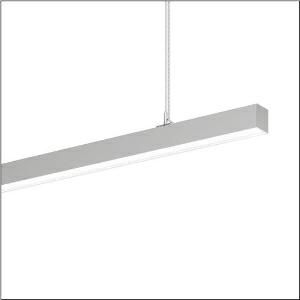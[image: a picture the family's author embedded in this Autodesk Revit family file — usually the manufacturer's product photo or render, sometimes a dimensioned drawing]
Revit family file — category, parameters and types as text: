
# Revit family: silica_r__21_51mx30dc39sb_d950
name_source: partatom
category: Lighting Fixtures
units: mm (PartAtom-declared; Revit-internal decimal feet)

## family parameters
Cut with Voids When Loaded = No
Host = Face
Light Source = No
Part Type = Normal
Room Calculation Point = No
Round Connector Dimension = Use Diameter
Shared = No

## types (1)
- --- (1 x LED, 10520 lm, 68.3 W, 3000K)
    Apparent Load = 68 VA
    CIE Flux Codes = 47 79 96 57 100
    Color Rendering = 80
    Color Temperature = 3000K
    Default Elevation = 1800 mm
    Description = Silica® 21, office luminaire, primary optical cover: cover, of PMMA, opal, light emission: direct/indirect distribution, primary light characteristic: symmetric, installation type: suspended mounting, LED, rated luminous flux: 10.520lm, luminous efficacy: 154lm/W, light colour: 830, colour temperature: 3000K, with terminal, 3+2-pole, max. 2.5mm², mains connection: 220..240V, AC, 50/60Hz, rated input power: 68.3W, luminaire housing, of aluminium, metallic grey (RAL 9006), length: 3.004mm, width: 53mm, height: 53mm, protection rating (complete): IP20, insulation class (complete): insulation class I (protective earthing), certification: CE, permissible operating ambient temperature: 0..+35°C, standard: EN 50419, packaging unit: 1 piece
    Height = 53 mm
    Lamp = 1 x LED
    Lamp Light Flux = 10520 lm
    Lamp Power = 68.3 W
    Lamp count = 1
    Length = 3004 mm
    Luminous efficacy = 154 lm/W
    Manufacturer = Siteco
    ModVariant = No
    Model = 51MX30DC39SB
    Mounting Place = Ceiling
    Mounting Type = Pendant
    Number of Poles = 1
    OnlyDefault = Yes
    Power Factor = 1
    Product Name = Silica® 21
    Product group = office luminaire | ceiling pendant
    ProductGroupID = 902
    Protection Class = Protection class I
    Protection Degree = IP 20
    RLX_Detail_Level = 1
    RLX_Emergency_Light_Flux = 0 lm
    RLX_Emergency_Type = 0
    RLX_Emergency_Type_DB = No
    RlxData = <blob elided: 23393 chars, md5=f553ad7e>
    Socket = socket
    Standby Power = 0 W
    System Light Flux = 10520 lm
    System Power = 68 W
    Type Comments = factory setting: luminous flux: 100 % | dim-lin: 254 | 233 mA
    Type Image = l_1313621.jpg
    URL = http://relux.com
    VarID = @adj_065259
    Voltage = 0 V
    Weight = 0.00 kg
    Width = 53 mm

## geometry (parser evidence)
native form markers: Blend x4, Sweep x13
no freeform markers — native parametric forms only
